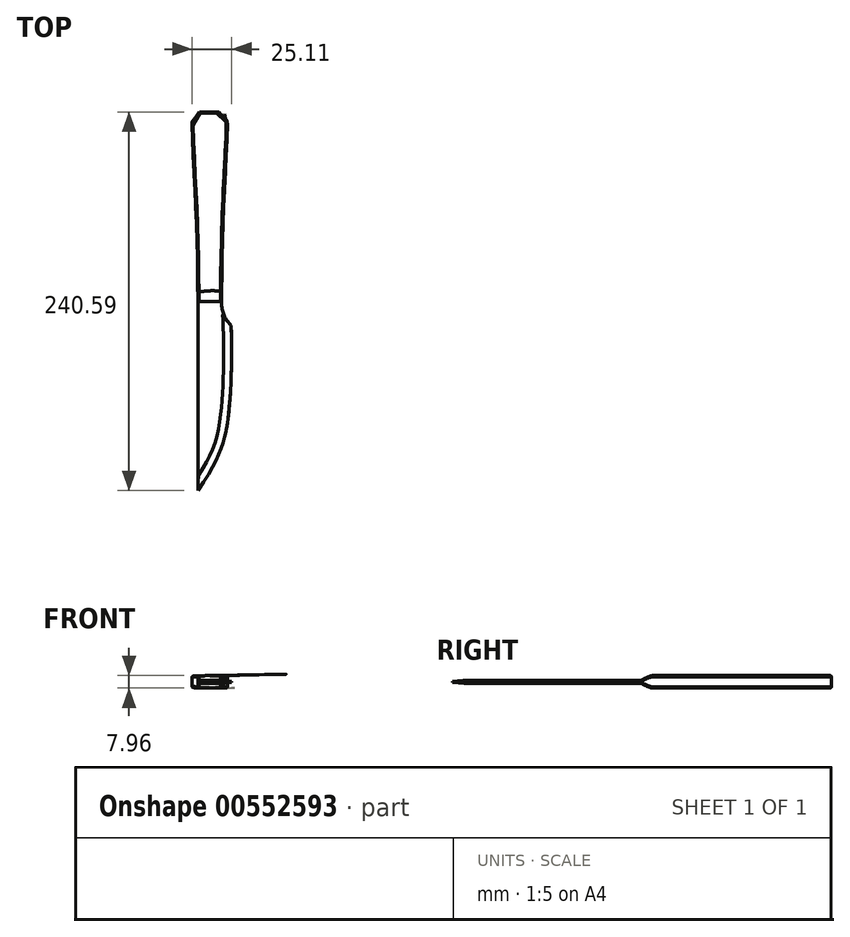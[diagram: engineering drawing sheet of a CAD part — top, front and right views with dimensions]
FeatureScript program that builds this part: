
annotation { "Feature Type Name" : "Feature", "Feature Type Description" : "" }
export const myFeature = defineFeature(function(context is Context, id is Id, definition is map)
    precondition{}
    {
        {
            var Q0;
            Q0=qCreatedBy(makeId("Top.planeOp"),FACE);
            var sketch = newSketch(context, id + "F0", { "sketchPlane" : qUnion([Q0])});
            skLineSegment(sketch, "E0", {"start": v(0, 0) * mm, "end": v(0, -120) * mm, "construction": true});
            skLineSegment(sketch, "E1", {"start": v(-14.5, 117.7) * mm, "end": v(7.5, 117.7) * mm, "construction": true});
            skPoint(sketch, "E2", {"position": v(-3.5, 117.7) * mm});
            skLineSegment(sketch, "E3", {"start": v(-12.5, 120) * mm, "end": v(5.5, 120) * mm, "construction": true});
            skPoint(sketch, "E4", {"position": v(-3.5, 120) * mm});
            skLineSegment(sketch, "E5", {"start": v(-11, -120) * mm, "end": v(11, -120) * mm, "construction": true});
            skPoint(sketch, "E6", {"position": v(0, -120) * mm});
            skLineSegment(sketch, "E7", {"start": v(-11, 0) * mm, "end": v(4, 0) * mm, "construction": true});
            skPoint(sketch, "E8", {"position": v(-3.5, 0) * mm});
            skPoint(sketch, "E9.visualSharp", {"position": v(-12.5, 120) * mm});
            skPoint(sketch, "E10.visualSharp", {"position": v(5.5, 120) * mm});
            skPoint(sketch, "E11.visualSharp", {"position": v(4, 0) * mm});
            skLineSegment(sketch, "E12", {"start": v(-11, -120) * mm, "end": v(-11, 0) * mm});
            skLineSegment(sketch, "E13", {"start": v(-3.5, 0) * mm, "end": v(-3.5, 120) * mm, "construction": true});
            skLineSegment(sketch, "E14", {"start": v(-12.5, 64) * mm, "end": v(5.5, 64) * mm, "construction": true});
            skPoint(sketch, "E15", {"position": v(-3.5, 64) * mm});
            skFitSpline(sketch, "E16", {"points": [v(-11, 0) * mm, v(-12.5, 64) * mm, v(-14.5, 117.7) * mm, v(-12.5, 120) * mm, v(5.5, 120) * mm, v(7.5, 117.7) * mm, v(5.5, 64) * mm, v(4, 0) * mm], "startDerivative": vector(-2.95, 288.04) * mm, "endDerivative": vector(-2.95, -288.04) * mm});
            skLineSegment(sketch, "E17", {"start": v(-3.5, 0) * mm, "end": v(-3.5, -120) * mm, "construction": true});
            skLineSegment(sketch, "E18", {"start": v(-11, -15) * mm, "end": v(10, -15) * mm, "construction": true});
            skArc(sketch, "E19", {"start": v(4, 0) * mm, "mid": v(5.42, -8.13) * mm, "end": v(10, -15) * mm});
            skLineSegment(sketch, "E20", {"start": v(-11, -75) * mm, "end": v(8, -75) * mm, "construction": true});
            skFitSpline(sketch, "E21", {"points": [v(10, -15) * mm, v(8, -75) * mm, v(-11, -120) * mm], "startDerivative": vector(5.73, -119.18) * mm, "endDerivative": vector(-88.15, -130.49) * mm});
            skLineSegment(sketch, "E22", {"start": v(8, -75) * mm, "end": v(-11, -120) * mm, "construction": true});
            skPoint(sketch, "E23", {"position": v(-1.5, -97.5) * mm});
            skLineSegment(sketch, "E24", {"start": v(-1.5, -97.5) * mm, "end": v(7.37, -101.24) * mm, "construction": true});
            skPoint(sketch, "E25", {"position": v(-11, -83) * mm});
            skLineSegment(sketch, "E26", {"start": v(4, 0) * mm, "end": v(-11, 0) * mm});
            skSolve(sketch);
        }
        {
            var Q0;
            Q0=makeQuery(id+"F0.imprint","IMPRINT",FACE,{"disambiguationData":[TD([[makeQuery(id+"F0.imprint","IMPRINT",EDGE,{"derivedFrom":sQuery(id+"F0.wireOp",EDGE,"E16")}),-1.0]])]});
            extrude(context, id + "F1", {"entities" : qUnion([Q0]), "depth" : 8 * mm, "offsetDistance" : 25 * mm, "symmetric" : true});
        }
        {
            var Q0;
            Q0=makeQuery(id+"F0.imprint","IMPRINT",FACE,{"disambiguationData":[TD([[makeQuery(id+"F0.imprint","IMPRINT",EDGE,{"derivedFrom":sQuery(id+"F0.wireOp",EDGE,"E12")}),-1.0]])]});
            extrude(context, id + "F2", {"entities" : qUnion([Q0]), "operationType" : NewBodyOperationType.ADD, "depth" : 2 * mm, "offsetDistance" : 25 * mm, "symmetric" : true});
        }
        {
            var Q0;
            Q0=makeQuery(id+"F1.opExtrude","CAP_EDGE",EDGE,{"disambiguationData":[OSD([sQuery(id+"F0.wireOp",EDGE,"E26")])],"isStart":false});
            var Q1;
            Q1=makeQuery(id+"F1.opExtrude","CAP_EDGE",EDGE,{"disambiguationData":[OSD([sQuery(id+"F0.wireOp",EDGE,"E26")])],"isStart":true});
            fillet(context, id + "F3", {"entities" : qUnion([Q0, Q1]), "radius" : 10 * mm, "tangentPropagation" : true, "rho" : 0.2, "crossSection" : FilletCrossSection.CONIC, "allowEdgeOverflow" : false});
        }
        {
            var Q0;
            Q0=makeQuery(id+"F2.opExtrude","CAP_EDGE",EDGE,{"disambiguationData":[OSD([sQuery(id+"F0.wireOp",EDGE,"E21")])],"isStart":false});
            var Q1;
            Q1=makeQuery(id+"F2.opExtrude","CAP_EDGE",EDGE,{"disambiguationData":[OSD([sQuery(id+"F0.wireOp",EDGE,"E21")])],"isStart":true});
            chamfer(context, id + "F4", {"entities" : qUnion([Q0, Q1]), "chamferType" : ChamferType.TWO_OFFSETS, "width1" : 0.8 * mm, "oppositeDirection" : false, "width2" : 5 * mm, "tangentPropagation" : true});
        }
        {
            var Q0;
            Q0=qCreatedBy(makeId("Front.planeOp"),FACE);
            cPlane(context, id + "F5", {"entities" : qUnion([Q0]), "cplaneType" : CPlaneType.OFFSET, "offset" : 130 * mm, "oppositeDirection" : true, "width" : 150 * mm, "height" : 150 * mm});
        }
        {
            var Q0;
            Q0=qCreatedBy(id+"F5.planeOp",FACE);
            var sketch = newSketch(context, id + "F6", { "sketchPlane" : qUnion([Q0])});
            skLineSegment(sketch, "E27", {"start": v(0, 2.76) * mm, "end": v(0, -2.76) * mm, "construction": true});
            skPoint(sketch, "E28", {"position": v(0, 0) * mm});
            skLineSegment(sketch, "E29", {"start": v(0, 0) * mm, "end": v(-20, 0) * mm, "construction": true});
            skLineSegment(sketch, "E30", {"start": v(0, 0) * mm, "end": v(16.5, 0) * mm, "construction": true});
            skLineSegment(sketch, "E31", {"start": v(16.5, 3.54) * mm, "end": v(16.5, -3.54) * mm, "construction": true});
            skLineSegment(sketch, "E32", {"start": v(-20, 3.54) * mm, "end": v(-20, -3.54) * mm, "construction": true});
            skPoint(sketch, "E33", {"position": v(16.5, 0) * mm});
            skPoint(sketch, "E34", {"position": v(-20, 0) * mm});
            skPoint(sketch, "E35", {"position": v(-3.5, 0) * mm});
            skArc(sketch, "E36", {"start": v(16.5, 3.24) * mm, "mid": v(-1.75, 3.98) * mm, "end": v(-20, 3.24) * mm});
            skArc(sketch, "E37", {"start": v(-20, -3.24) * mm, "mid": v(-1.75, -3.98) * mm, "end": v(16.5, -3.24) * mm});
            skLineSegment(sketch, "E38.bottom", {"start": v(20.2, 11.75) * mm, "end": v(-24.27, 11.75) * mm});
            skLineSegment(sketch, "E38.top", {"start": v(20.2, -15.43) * mm, "end": v(-24.27, -15.43) * mm});
            skLineSegment(sketch, "E38.left", {"start": v(20.2, 11.75) * mm, "end": v(20.2, -15.43) * mm});
            skLineSegment(sketch, "E38.right", {"start": v(-24.27, 11.75) * mm, "end": v(-24.27, -15.43) * mm});
            skLineSegment(sketch, "E39", {"start": v(-3.5, 0) * mm, "end": v(-3.5, 3.98) * mm, "construction": true});
            skLineSegment(sketch, "E40", {"start": v(-3.5, 0) * mm, "end": v(-3.5, -3.98) * mm, "construction": true});
            skLineSegment(sketch, "E41", {"start": v(-20, 3.24) * mm, "end": v(-20, -3.24) * mm});
            skLineSegment(sketch, "E42", {"start": v(16.5, 3.24) * mm, "end": v(16.5, -3.24) * mm});
            skSolve(sketch);
        }
        {
            var Q0;
            {var subQ1=sQuery(id+"F6.wireOp",EDGE,"iI0NrAip-O41P-A39r-DtJV-qbhLXR6NnK21");Q0=makeQuery(id+"F6.imprint","IMPRINT",FACE,{"disambiguationData":[TD([[makeQuery(id+"F6.imprint","IMPRINT",EDGE,{"derivedFrom":subQ1}),-1.0]])]});}
            var Q1;
            Q1=makeQuery(id+"F6.imprint","IMPRINT",FACE,{"disambiguationData":[TD([[makeQuery(id+"F6.imprint","IMPRINT",EDGE,{"derivedFrom":sQuery(id+"F6.wireOp",EDGE,"E36")}),-1.0]])]});
            extrude(context, id + "F7", {"entities" : qUnion([Q0, Q1]), "operationType" : NewBodyOperationType.REMOVE, "depth" : 125 * mm, "offsetDistance" : 25 * mm});
        }
        {
            var Q0;
            Q0=makeQuery(id+"F2.opExtrude","CAP_EDGE",EDGE,{"disambiguationData":[OSD([sQuery(id+"F0.wireOp",EDGE,"E19")])],"isStart":false});
            var Q1;
            Q1=makeQuery(id+"F2.opExtrude","CAP_EDGE",EDGE,{"disambiguationData":[OSD([sQuery(id+"F0.wireOp",EDGE,"E19")])],"isStart":true});
            fillet(context, id + "F8", {"entities" : qUnion([Q0, Q1]), "radius" : 0.8 * mm, "tangentPropagation" : true, "allowEdgeOverflow" : false});
        }
        {
            var Q0;
            Q0=makeQuery(id+"F7.boolean.opBoolean","INTERSECT",EDGE,{"derivedFrom":[makeQuery(id+"F1.opExtrude","SWEPT_FACE",FACE,{"disambiguationData":[OSD([sQuery(id+"F0.wireOp",EDGE,"E16")])]}),makeQuery(id+"F7.opExtrude","SWEPT_FACE",FACE,{"disambiguationData":[OSD([sQuery(id+"F6.wireOp",EDGE,"E37")])]})]});
            var Q1;
            Q1=makeQuery(id+"F3.opFillet","BLEND_EDGE",EDGE,{"disambiguationData":[OD(0.0)],"blendedFrom":[makeQuery(id+"F1.opExtrude","CAP_EDGE",EDGE,{"disambiguationData":[OSD([sQuery(id+"F0.wireOp",EDGE,"E26")])],"isStart":true}),makeQuery(id+"F1.opExtrude","SWEPT_FACE",FACE,{"disambiguationData":[OSD([sQuery(id+"F0.wireOp",EDGE,"E16")])]})],"blendedInto":[makeQuery(id+"F1.opExtrude","SWEPT_FACE",FACE,{"disambiguationData":[OSD([sQuery(id+"F0.wireOp",EDGE,"E16")])]})]});
            var Q2;
            Q2=makeQuery(id+"F3.opFillet","BLEND_EDGE",EDGE,{"disambiguationData":[OD(1.0)],"blendedFrom":[makeQuery(id+"F1.opExtrude","CAP_EDGE",EDGE,{"disambiguationData":[OSD([sQuery(id+"F0.wireOp",EDGE,"E26")])],"isStart":true}),makeQuery(id+"F1.opExtrude","SWEPT_FACE",FACE,{"disambiguationData":[OSD([sQuery(id+"F0.wireOp",EDGE,"E16")])]})],"blendedInto":[makeQuery(id+"F1.opExtrude","SWEPT_FACE",FACE,{"disambiguationData":[OSD([sQuery(id+"F0.wireOp",EDGE,"E16")])]})]});
            var Q3;
            Q3=makeQuery(id+"F3.opFillet","BLEND_EDGE",EDGE,{"disambiguationData":[OD(1.0)],"blendedFrom":[makeQuery(id+"F1.opExtrude","CAP_EDGE",EDGE,{"disambiguationData":[OSD([sQuery(id+"F0.wireOp",EDGE,"E26")])],"isStart":false}),makeQuery(id+"F1.opExtrude","SWEPT_FACE",FACE,{"disambiguationData":[OSD([sQuery(id+"F0.wireOp",EDGE,"E16")])]})],"blendedInto":[makeQuery(id+"F1.opExtrude","SWEPT_FACE",FACE,{"disambiguationData":[OSD([sQuery(id+"F0.wireOp",EDGE,"E16")])]})]});
            var Q4;
            Q4=makeQuery(id+"F3.opFillet","BLEND_EDGE",EDGE,{"disambiguationData":[OD(0.0)],"blendedFrom":[makeQuery(id+"F1.opExtrude","CAP_EDGE",EDGE,{"disambiguationData":[OSD([sQuery(id+"F0.wireOp",EDGE,"E26")])],"isStart":false}),makeQuery(id+"F1.opExtrude","SWEPT_FACE",FACE,{"disambiguationData":[OSD([sQuery(id+"F0.wireOp",EDGE,"E16")])]})],"blendedInto":[makeQuery(id+"F1.opExtrude","SWEPT_FACE",FACE,{"disambiguationData":[OSD([sQuery(id+"F0.wireOp",EDGE,"E16")])]})]});
            var Q5;
            Q5=makeQuery(id+"F7.boolean.opBoolean","INTERSECT",EDGE,{"derivedFrom":[makeQuery(id+"F1.opExtrude","SWEPT_FACE",FACE,{"disambiguationData":[OSD([sQuery(id+"F0.wireOp",EDGE,"E16")])]}),makeQuery(id+"F7.opExtrude","SWEPT_FACE",FACE,{"disambiguationData":[OSD([sQuery(id+"F6.wireOp",EDGE,"E36")])]})]});
            var Q6;
            Q6=makeQuery(id+"F2.opExtrude","CAP_EDGE",EDGE,{"disambiguationData":[OSD([sQuery(id+"F0.wireOp",EDGE,"E12")])],"isStart":true});
            var Q7;
            Q7=makeQuery(id+"F2.opExtrude","CAP_EDGE",EDGE,{"disambiguationData":[OSD([sQuery(id+"F0.wireOp",EDGE,"E12")])],"isStart":false});
            fillet(context, id + "F9", {"entities" : qUnion([Q0, Q1, Q2, Q3, Q4, Q5, Q6, Q7]), "radius" : 0.7 * mm, "tangentPropagation" : true, "allowEdgeOverflow" : false});
        }
    });
